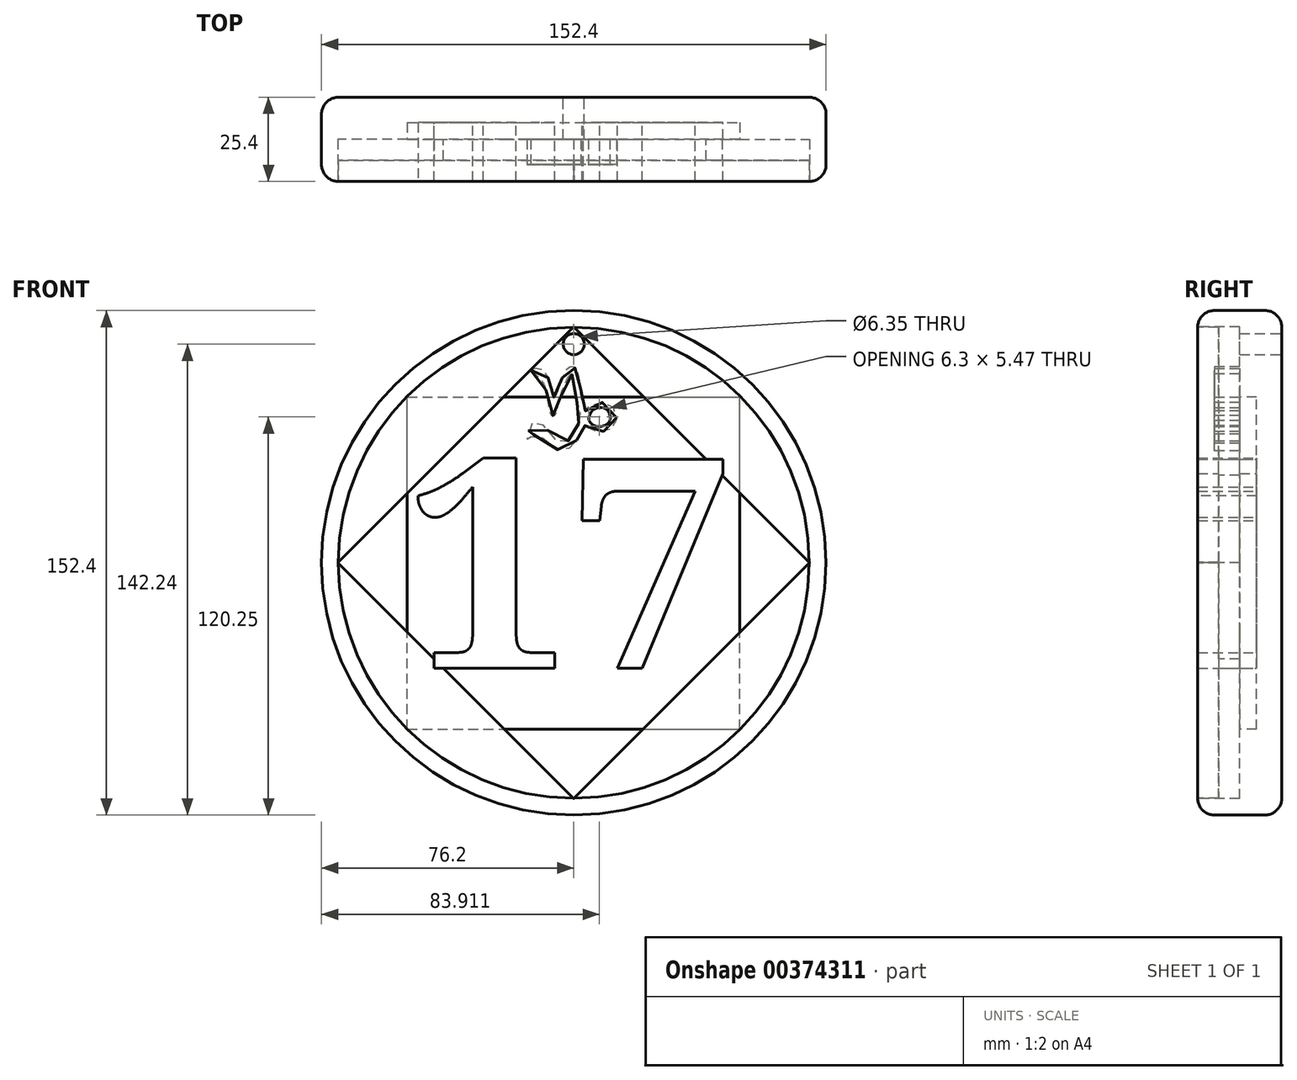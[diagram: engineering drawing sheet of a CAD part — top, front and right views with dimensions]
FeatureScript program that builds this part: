
annotation { "Feature Type Name" : "Feature", "Feature Type Description" : "" }
export const myFeature = defineFeature(function(context is Context, id is Id, definition is map)
    precondition{}
    {
        {
            var Q0;
            Q0=qCreatedBy(makeId("Front.planeOp"),FACE);
            var sketch = newSketch(context, id + "F0", { "sketchPlane" : qUnion([Q0])});
            skCircle(sketch, "E0", {"center": v(0, 0) * mm, "radius": 76.2 * mm});
            skSolve(sketch);
        }
        {
            var Q0;
            Q0 = qSketchRegion(id + "F0", true);
            extrude(context, id + "F1", {"entities" : qUnion([Q0]), "depth" : 25.4 * mm});
        }
        {
            var Q0;
            Q0=makeQuery(id+"F1.opExtrude","CAP_EDGE",EDGE,{"disambiguationData":[OSD([sQuery(id+"F0.wireOp",EDGE,"E0")])],"isStart":false});
            fillet(context, id + "F2", {"entities" : qUnion([Q0]), "radius" : 5.08 * mm, "tangentPropagation" : true, "allowEdgeOverflow" : false});
        }
        {
            var Q0;
            Q0=makeQuery(id+"F1.opExtrude","CAP_EDGE",EDGE,{"disambiguationData":[OSD([sQuery(id+"F0.wireOp",EDGE,"E0")])],"isStart":true});
            fillet(context, id + "F3", {"entities" : qUnion([Q0]), "radius" : 5.08 * mm, "tangentPropagation" : true, "allowEdgeOverflow" : false});
        }
        {
            var Q0;
            Q0=qCreatedBy(makeId("Front.planeOp"),FACE);
            var sketch = newSketch(context, id + "F4", { "sketchPlane" : qUnion([Q0])});
            skCircle(sketch, "E1", {"center": v(0, 66.04) * mm, "radius": 3.18 * mm});
            skSolve(sketch);
        }
        {
            var Q0;
            Q0=sQuery(id+"F4.wireOp",VERTEX,"E1.center");
            var Q1;
            Q1=makeQuery(id+"F1.opExtrude","SWEPT_BODY",BODY,{"disambiguationData":[OSD([sQuery(id+"F0.wireOp",EDGE,"E0")])]});
            hole(context, id + "F5", {"style" : HoleStyle.SIMPLE, "endStyle" : HoleEndStyle.THROUGH, "oppositeDirection" : true, "holeDiameter" : 6.35 * mm, "isTappedThrough" : true, "tappedDepth" : 12.7 * mm, "tapClearance" : 3, "locations" : qUnion([Q0]), "scope" : qUnion([Q1])});
        }
        {
            var Q0;
            Q0=makeQuery(id+"F0.imprint","IMPRINT",FACE,{"disambiguationData":[TD([[makeQuery(id+"F0.imprint","IMPRINT",EDGE,{"derivedFrom":sQuery(id+"F0.wireOp",EDGE,"E0")}),1.0]])]});
            var sketch = newSketch(context, id + "F6", { "sketchPlane" : qUnion([Q0])});
            skText(sketch, "E2", { "text": "17", "fontName": "NotoSerif-Bold.ttf"});
            const initialGuessF6  = {"E2": [-0.0508, -0.03181, 1, 0, 0.06362]};
            skSetInitialGuess(sketch, initialGuessF6);
            skSolve(sketch);
        }
        {
            var Q0;
            Q0=makeQuery(id+"F0.imprint","IMPRINT",FACE,{"disambiguationData":[TD([[makeQuery(id+"F0.imprint","IMPRINT",EDGE,{"derivedFrom":sQuery(id+"F0.wireOp",EDGE,"E0")}),1.0]])]});
            var sketch = newSketch(context, id + "F7", { "sketchPlane" : qUnion([Q0])});
            skPoint(sketch, "E3.19.internal.snap0", {"position": v(0, 62.67) * mm});
            skFitSpline(sketch, "E3", {"points": [v(-12.94, 58.17) * mm, v(-9.4, 54.6) * mm, v(-6.87, 44.68) * mm, v(-5.53, 44.77) * mm, v(-4.73, 47.9) * mm, v(-0.82, 57) * mm, v(0.36, 51.28) * mm, v(2.06, 43.7) * mm, v(0.9, 41.1) * mm, v(-1.43, 37.08) * mm, v(-4.82, 36.64) * mm, v(-11.79, 42.9) * mm, v(-14.1, 36.74) * mm, v(-11.97, 38.79) * mm, v(-4.64, 34.05) * mm, v(0, 35.92) * mm, v(2.15, 39.4) * mm, v(3.3, 41.46) * mm, v(5.1, 40.12) * mm, v(11.34, 40.47) * mm, v(12.86, 43.68) * mm, v(10.81, 47.97) * mm, v(4.74, 47.26) * mm, v(3.58, 45.83) * mm, v(2.24, 50.39) * mm, v(1.26, 57.53) * mm, v(0, 59.05) * mm, v(-2.05, 58.43) * mm, v(-4.82, 52.1) * mm, v(-6.1, 50.04) * mm, v(-6.77, 52) * mm, v(-9.5, 58.17) * mm, v(-12.94, 58.17) * mm]});
            skSolve(sketch);
        }
        {
            var Q0;
            Q0=makeQuery(id+"F1.opExtrude","CAP_FACE",FACE,{"disambiguationData":[OSD([sQuery(id+"F0.wireOp",EDGE,"E0")])],"isStart":false});
            var sketch = newSketch(context, id + "F8", { "sketchPlane" : qUnion([Q0])});
            skFitSpline(sketch, "E4", {"points": [v(4.56, 43.02) * mm, v(4.83, 44.82) * mm, v(6.15, 46.4) * mm, v(8.47, 46.88) * mm, v(10.11, 46.14) * mm, v(10.9, 44.5) * mm, v(10.9, 42.97) * mm, v(9.85, 41.76) * mm, v(8.1, 41.17) * mm, v(6.1, 41.5) * mm, v(4.56, 43.02) * mm]});
            skSolve(sketch);
        }
        {
            var Q0;
            Q0=makeQuery(id+"F1.opExtrude","CAP_FACE",FACE,{"disambiguationData":[OSD([sQuery(id+"F0.wireOp",EDGE,"E0")])],"isStart":false});
            var sketch = newSketch(context, id + "F9", { "sketchPlane" : qUnion([Q0])});
            skLineSegment(sketch, "E5.0", {"start": v(0, -71.27) * mm, "end": v(-71.27, 0) * mm});
            skLineSegment(sketch, "E5.1", {"start": v(-71.27, 0) * mm, "end": v(0, 71.27) * mm});
            skLineSegment(sketch, "E5.2", {"start": v(0, 71.27) * mm, "end": v(71.27, 0) * mm});
            skLineSegment(sketch, "E5.3", {"start": v(71.27, 0) * mm, "end": v(0, -71.27) * mm});
            skSolve(sketch);
        }
        {
            var Q0;
            Q0=makeQuery(id+"F1.opExtrude","CAP_FACE",FACE,{"disambiguationData":[OSD([sQuery(id+"F0.wireOp",EDGE,"E0")])],"isStart":false});
            var sketch = newSketch(context, id + "F10", { "sketchPlane" : qUnion([Q0])});
            skCircle(sketch, "E6", {"center": v(0, 0) * mm, "radius": 71.12 * mm});
            skSolve(sketch);
        }
        {
            var Q0;
            Q0 = qSketchRegion(id + "F10", true);
            extrude(context, id + "F11", {"entities" : qUnion([Q0]), "operationType" : NewBodyOperationType.REMOVE, "oppositeDirection" : true, "depth" : 6.35 * mm});
        }
        {
            var Q0;
            Q0 = qSketchRegion(id + "F9", true);
            extrude(context, id + "F12", {"entities" : qUnion([Q0]), "operationType" : NewBodyOperationType.REMOVE, "oppositeDirection" : true, "depth" : 12.7 * mm});
        }
        {
            var Q0;
            Q0 = qSketchRegion(id + "F7", true);
            extrude(context, id + "F13", {"entities" : qUnion([Q0]), "operationType" : NewBodyOperationType.ADD, "depth" : 20.32 * mm});
        }
        {
            var Q0;
            Q0=makeQuery(id+"F12.boolean.opBoolean","COPY",FACE,{"derivedFrom":makeQuery(id+"F12.opExtrude","CAP_FACE",FACE,{"disambiguationData":[OSD([sQuery(id+"F9.wireOp",EDGE,"E5.0"),sQuery(id+"F9.wireOp",EDGE,"E5.1"),sQuery(id+"F9.wireOp",EDGE,"E5.2"),sQuery(id+"F9.wireOp",EDGE,"E5.3")])],"isStart":false})});
            var sketch = newSketch(context, id + "F14", { "sketchPlane" : qUnion([Q0])});
            skLineSegment(sketch, "E7.bottom", {"start": v(-50.29, -50.29) * mm, "end": v(50.08, -50.29) * mm});
            skLineSegment(sketch, "E7.top", {"start": v(-50.29, 50.08) * mm, "end": v(50.08, 50.08) * mm});
            skLineSegment(sketch, "E7.left", {"start": v(-50.29, -50.29) * mm, "end": v(-50.29, 50.08) * mm});
            skLineSegment(sketch, "E7.right", {"start": v(50.08, -50.29) * mm, "end": v(50.08, 50.08) * mm});
            skSolve(sketch);
        }
        {
            var Q0;
            Q0 = qSketchRegion(id + "F14", true);
            extrude(context, id + "F15", {"entities" : qUnion([Q0]), "operationType" : NewBodyOperationType.REMOVE, "oppositeDirection" : true, "depth" : 5.08 * mm});
        }
        {
            var Q0;
            Q0 = qSketchRegion(id + "F8", true);
            extrude(context, id + "F16", {"entities" : qUnion([Q0]), "operationType" : NewBodyOperationType.REMOVE, "oppositeDirection" : true, "depth" : 17.78 * mm});
        }
        {
            var Q0;
            Q0 = qSketchRegion(id + "F6", true);
            extrude(context, id + "F17", {"entities" : qUnion([Q0]), "operationType" : NewBodyOperationType.ADD, "depth" : 25.4 * mm});
        }
    });
